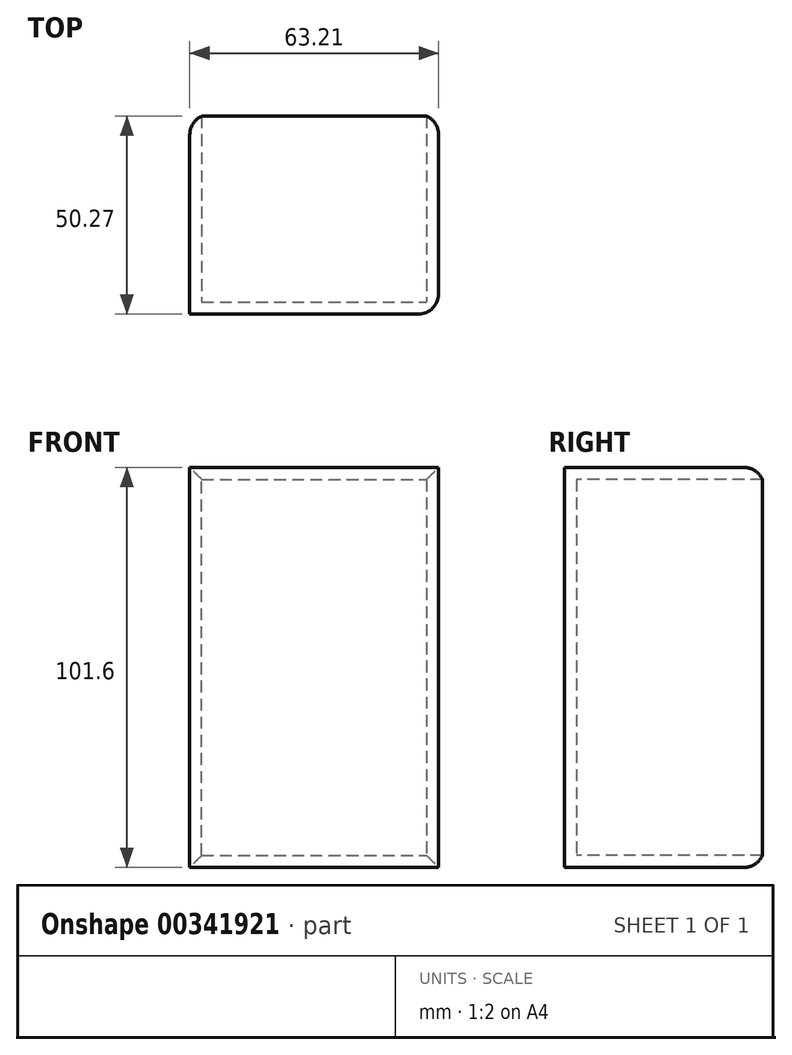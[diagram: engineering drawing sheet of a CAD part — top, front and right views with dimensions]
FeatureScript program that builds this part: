
annotation { "Feature Type Name" : "Feature", "Feature Type Description" : "" }
export const myFeature = defineFeature(function(context is Context, id is Id, definition is map)
    precondition{}
    {
        {
            var Q0;
            Q0=qCreatedBy(makeId("Top.planeOp"),FACE);
            var sketch = newSketch(context, id + "F0", { "sketchPlane" : qUnion([Q0])});
            skLineSegment(sketch, "E0.bottom", {"start": v(0, 0) * mm, "end": v(63.21, 0) * mm});
            skLineSegment(sketch, "E0.top", {"start": v(0, -50.69) * mm, "end": v(63.21, -50.69) * mm});
            skLineSegment(sketch, "E0.left", {"start": v(0, 0) * mm, "end": v(0, -50.69) * mm});
            skLineSegment(sketch, "E0.right", {"start": v(63.21, 0) * mm, "end": v(63.21, -50.69) * mm});
            skSolve(sketch);
        }
        {
            var Q0;
            Q0=makeQuery(id+"F0.imprint","IMPRINT",FACE,{"disambiguationData":[TD([[makeQuery(id+"F0.imprint","IMPRINT",EDGE,{"derivedFrom":sQuery(id+"F0.wireOp",EDGE,"E0.bottom")}),-1.0]])]});
            extrude(context, id + "F1", {"entities" : qUnion([Q0]), "depth" : 101.6 * mm});
        }
        {
            var Q0;
            Q0=makeQuery(id+"F1.opExtrude","SWEPT_FACE",FACE,{"disambiguationData":[OSD([sQuery(id+"F0.wireOp",EDGE,"E0.bottom")])]});
            shell(context, id + "F2", {"entities" : qUnion([Q0]), "thickness" : 3.05 * mm});
        }
        {
            var Q0;
            Q0=makeQuery(id+"F1.opExtrude","SWEPT_EDGE",EDGE,{"disambiguationData":[OSD([sQuery(id+"F0.wireOp",EDGE,"E0.bottom"),sQuery(id+"F0.wireOp",EDGE,"E0.left")])]});
            var Q1;
            Q1=makeQuery(id+"F1.opExtrude","CAP_EDGE",EDGE,{"disambiguationData":[OSD([sQuery(id+"F0.wireOp",EDGE,"E0.bottom")])],"isStart":false});
            var Q2;
            Q2=makeQuery(id+"F1.opExtrude","SWEPT_EDGE",EDGE,{"disambiguationData":[OSD([sQuery(id+"F0.wireOp",EDGE,"E0.bottom"),sQuery(id+"F0.wireOp",EDGE,"E0.right")])]});
            var Q3;
            Q3=makeQuery(id+"F1.opExtrude","CAP_EDGE",EDGE,{"disambiguationData":[OSD([sQuery(id+"F0.wireOp",EDGE,"E0.bottom")])],"isStart":true});
            var Q4;
            Q4=makeQuery(id+"F1.opExtrude","SWEPT_EDGE",EDGE,{"disambiguationData":[OSD([sQuery(id+"F0.wireOp",EDGE,"E0.top"),sQuery(id+"F0.wireOp",EDGE,"E0.right")])]});
            fillet(context, id + "F3", {"entities" : qUnion([Q0, Q1, Q2, Q3, Q4]), "radius" : 5.08 * mm, "tangentPropagation" : true, "allowEdgeOverflow" : false});
        }
    });
